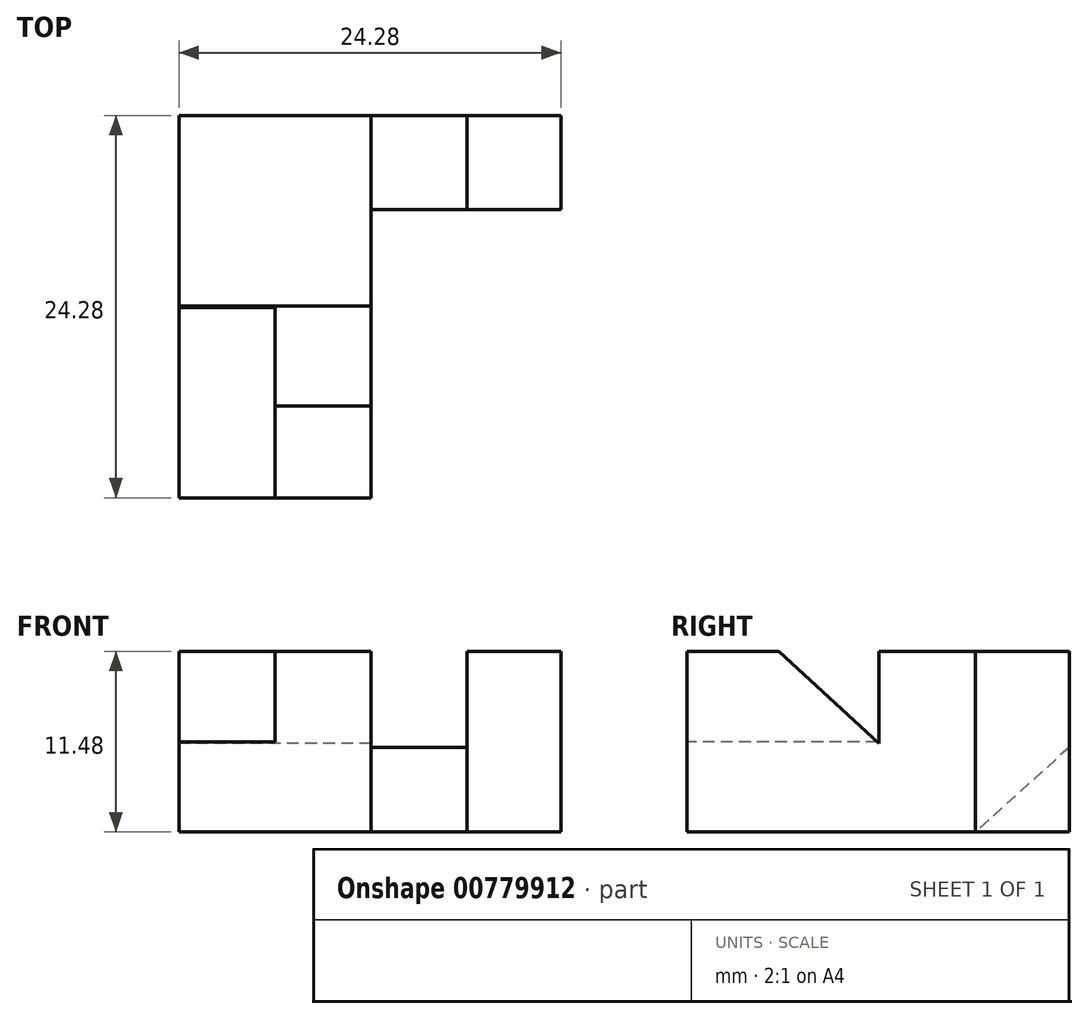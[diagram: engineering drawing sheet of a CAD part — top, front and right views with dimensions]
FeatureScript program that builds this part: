
annotation { "Feature Type Name" : "Feature", "Feature Type Description" : "" }
export const myFeature = defineFeature(function(context is Context, id is Id, definition is map)
    precondition{}
    {
        {
            var Q0;
            Q0=qCreatedBy(makeId("Top.planeOp"),FACE);
            var sketch = newSketch(context, id + "F0", { "sketchPlane" : qUnion([Q0])});
            skLineSegment(sketch, "E0", {"start": v(0, 0) * mm, "end": v(24.28, 0) * mm});
            skLineSegment(sketch, "E1", {"start": v(24.28, 0) * mm, "end": v(24.28, -5.97) * mm});
            skLineSegment(sketch, "E2", {"start": v(24.28, -5.97) * mm, "end": v(18.31, -5.97) * mm});
            skLineSegment(sketch, "E3", {"start": v(18.31, -5.97) * mm, "end": v(12.22, -5.97) * mm});
            skLineSegment(sketch, "E4", {"start": v(0, 0) * mm, "end": v(0, -24.28) * mm});
            skLineSegment(sketch, "E5", {"start": v(0, -24.28) * mm, "end": v(12.22, -24.28) * mm});
            skLineSegment(sketch, "E6", {"start": v(12.22, -24.28) * mm, "end": v(12.22, -5.97) * mm});
            skSolve(sketch);
        }
        {
            var Q0;
            Q0 = qSketchRegion(id + "F0", true);
            extrude(context, id + "F1", {"entities" : qUnion([Q0]), "depth" : 11.48 * mm, "offsetDistance" : 25.4 * mm});
        }
        {
            var Q0;
            Q0=qCreatedBy(makeId("Right.planeOp"),FACE);
            var sketch = newSketch(context, id + "F2", { "sketchPlane" : qUnion([Q0])});
            skLineSegment(sketch, "E7", {"start": v(0, 11.48) * mm, "end": v(-12.1, 11.48) * mm});
            skLineSegment(sketch, "E8", {"start": v(-24.28, 11.48) * mm, "end": v(-18.44, 11.48) * mm});
            skLineSegment(sketch, "E9", {"start": v(-12.1, 5.63) * mm, "end": v(-18.44, 11.48) * mm});
            skLineSegment(sketch, "E10", {"start": v(-12.1, 5.63) * mm, "end": v(-12.1, 11.48) * mm});
            skLineSegment(sketch, "E11", {"start": v(-12.1, 11.48) * mm, "end": v(-18.44, 11.48) * mm});
            skLineSegment(sketch, "E12", {"start": v(-24.28, 11.48) * mm, "end": v(-24.28, 0) * mm});
            skSolve(sketch);
        }
        {
            var Q0;
            Q0=makeQuery(id+"F2.imprint","IMPRINT",FACE,{"disambiguationData":[TD([[makeQuery(id+"F2.imprint","IMPRINT",EDGE,{"derivedFrom":sQuery(id+"F2.wireOp",EDGE,"E9")}),-1.0]])]});
            var Q1;
            Q1=makeQuery(id+"F1.opExtrude","SWEPT_FACE",FACE,{"disambiguationData":[OSD([sQuery(id+"F0.wireOp",EDGE,"E6")])]});
            extrude(context, id + "F3", {"entities" : qUnion([Q0]), "operationType" : NewBodyOperationType.REMOVE, "endBound" : BoundingType.UP_TO_SURFACE, "depth" : 25.4 * mm, "endBoundEntityFace" : qUnion([Q1]), "offsetDistance" : 25.4 * mm});
        }
        {
            var Q0;
            Q0=makeQuery(id+"F1.opExtrude","SWEPT_FACE",FACE,{"disambiguationData":[OSD([sQuery(id+"F0.wireOp",EDGE,"E5")])]});
            var sketch = newSketch(context, id + "F4", { "sketchPlane" : qUnion([Q0])});
            skLineSegment(sketch, "E13", {"start": v(0, 0) * mm, "end": v(0, 5.72) * mm});
            skLineSegment(sketch, "E14", {"start": v(0, 11.48) * mm, "end": v(0, 5.72) * mm});
            skLineSegment(sketch, "E15", {"start": v(0, 11.48) * mm, "end": v(6.1, 11.48) * mm});
            skLineSegment(sketch, "E16", {"start": v(12.2, 11.48) * mm, "end": v(6.1, 11.48) * mm});
            skLineSegment(sketch, "E17", {"start": v(18.29, 11.48) * mm, "end": v(12.2, 11.48) * mm});
            skLineSegment(sketch, "E18", {"start": v(18.29, 11.48) * mm, "end": v(24.28, 11.48) * mm});
            skLineSegment(sketch, "E19", {"start": v(12.2, 11.48) * mm, "end": v(12.2, 5.38) * mm});
            skLineSegment(sketch, "E20", {"start": v(12.2, 5.38) * mm, "end": v(18.29, 5.38) * mm});
            skLineSegment(sketch, "E21", {"start": v(18.29, 5.38) * mm, "end": v(18.29, 11.48) * mm});
            skLineSegment(sketch, "E22", {"start": v(0, 5.72) * mm, "end": v(6.1, 5.72) * mm});
            skLineSegment(sketch, "E23", {"start": v(6.1, 5.72) * mm, "end": v(6.1, 11.48) * mm});
            skLineSegment(sketch, "E24.right", {"start": v(6.1, 11.48) * mm, "end": v(6.1, 5.72) * mm});
            skSolve(sketch);
        }
        {
            var Q0;
            Q0=makeQuery(id+"F4.imprint","IMPRINT",FACE,{"disambiguationData":[TD([[makeQuery(id+"F4.imprint","IMPRINT",EDGE,{"derivedFrom":sQuery(id+"F4.wireOp",EDGE,"E15")}),-1.0]])]});
            var Q1;
            Q1=makeQuery(id+"F3.boolean.opBoolean","COPY",FACE,{"derivedFrom":makeQuery(id+"F3.opExtrude","SWEPT_FACE",FACE,{"disambiguationData":[OSD([sQuery(id+"F2.wireOp",EDGE,"E10")])]})});
            extrude(context, id + "F5", {"entities" : qUnion([Q0]), "operationType" : NewBodyOperationType.REMOVE, "endBound" : BoundingType.UP_TO_SURFACE, "oppositeDirection" : true, "depth" : 25.4 * mm, "endBoundEntityFace" : qUnion([Q1]), "offsetDistance" : 25.4 * mm});
        }
        {
            var Q0;
            {var subQ3=sQuery(id+"F4.wireOp",EDGE,"E21");Q0=makeQuery(id+"F4.imprint","IMPRINT",FACE,{"disambiguationData":[TD([[makeQuery(id+"F4.imprint","IMPRINT",EDGE,{"derivedFrom":subQ3}),1.0]])]});}
            extrude(context, id + "F6", {"entities" : qUnion([Q0]), "operationType" : NewBodyOperationType.REMOVE, "oppositeDirection" : true, "depth" : 25.4 * mm, "offsetDistance" : 25.4 * mm});
        }
        {
            var Q0;
            Q0=makeQuery(id+"F1.opExtrude","SWEPT_FACE",FACE,{"disambiguationData":[OSD([sQuery(id+"F0.wireOp",EDGE,"E1")])]});
            var sketch = newSketch(context, id + "F7", { "sketchPlane" : qUnion([Q0])});
            skLineSegment(sketch, "E25", {"start": v(0, 0) * mm, "end": v(0, 5.38) * mm});
            skLineSegment(sketch, "E26", {"start": v(0, 5.38) * mm, "end": v(-5.97, 0) * mm});
            skLineSegment(sketch, "E27", {"start": v(-5.97, 0) * mm, "end": v(0, 0) * mm});
            skLineSegment(sketch, "E28", {"start": v(0, 5.38) * mm, "end": v(-5.97, 5.38) * mm});
            skLineSegment(sketch, "E29", {"start": v(-5.97, 5.38) * mm, "end": v(-5.97, 0) * mm});
            skSolve(sketch);
        }
        {
            var Q0;
            Q0=makeQuery(id+"F7.imprint","IMPRINT",FACE,{"disambiguationData":[TD([[makeQuery(id+"F7.imprint","IMPRINT",EDGE,{"derivedFrom":sQuery(id+"F7.wireOp",EDGE,"E26")}),-1.0]])]});
            var Q1;
            {var subQ0=sQuery(id+"F0.wireOp",EDGE,"E6");Q1=makeQuery(id+"F6.boolean.opBoolean","MERGE",FACE,{"derivedFrom":[makeQuery(id+"F1.opExtrude","SWEPT_FACE",FACE,{"disambiguationData":[OSD([subQ0])]}),makeQuery(id+"F6.opExtrude","SWEPT_FACE",FACE,{"disambiguationData":[OSD([sQuery(id+"F0.wireOp",EDGE,"E5"),subQ0])]})]});}
            var Q2;
            Q2=makeQuery(id+"F6.boolean.opBoolean","COPY",FACE,{"derivedFrom":makeQuery(id+"F6.opExtrude","SWEPT_FACE",FACE,{"disambiguationData":[OSD([sQuery(id+"F4.wireOp",EDGE,"E21")])]})});
            extrude(context, id + "F8", {"entities" : qUnion([Q0]), "operationType" : NewBodyOperationType.REMOVE, "endBound" : BoundingType.UP_TO_SURFACE, "oppositeDirection" : true, "depth" : 25.4 * mm, "endBoundEntityFace" : qUnion([Q1]), "offsetDistance" : 25.4 * mm, "hasSecondDirection" : true, "secondDirectionBound" : SecondDirectionBoundingType.UP_TO_SURFACE, "secondDirectionOppositeDirection" : true, "secondDirectionDepth" : 25.4 * mm, "secondDirectionBoundEntityFace" : qUnion([Q2])});
        }
    });
